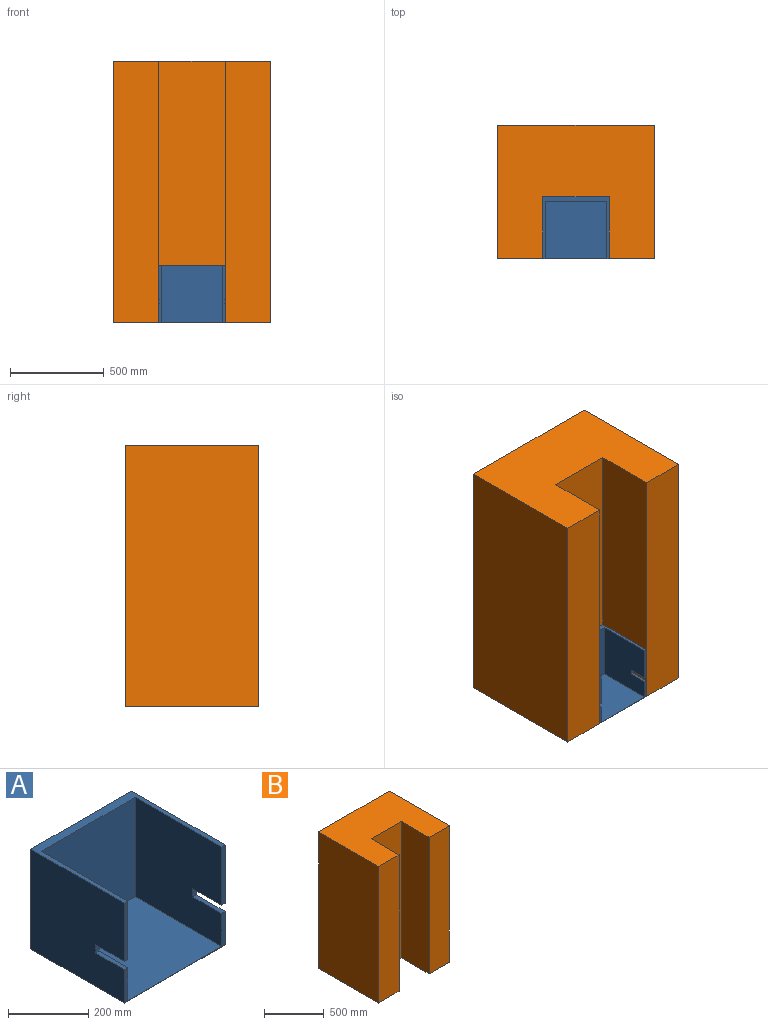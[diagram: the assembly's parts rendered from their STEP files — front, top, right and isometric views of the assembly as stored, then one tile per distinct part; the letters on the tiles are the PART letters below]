
ASSEMBLY  parts=2 mates=1
PART A: 18 faces, bbox 355.6x330.2x304.8 mm
  f0: plane 177.8x12.7mm, normal (0,-1,0), area 2258.1mm2, adj f2,f3,f11,f16
  f1: plane 177.8x12.7mm, normal (0,-1,0), area 2258.1mm2, adj f4,f5,f11,f13
  f2: plane 330.2x304.8mm, normal (1,0,0), area 98064.3mm2, adj f0,f6,f7,f9,f11,f15,f16,f17
  f3: plane 304.8x303.21mm, normal (-1,0,0), area 89838.5mm2, adj f0,f6,f8,f10,f11,f15,f16,f17
  f4: plane 304.8x303.21mm, normal (1,0,0), area 89838.5mm2, adj f1,f6,f8,f10,f11,f12,f13,f14
  f5: plane 330.2x304.8mm, normal (-1,0,0), area 98064.3mm2, adj f1,f6,f7,f9,f11,f12,f13,f14
  f6: plane 355.6x101.6mm, normal (0,-1,0), area 3104.8mm2, adj f2,f3,f4,f5,f8,f9,f14,f15
  f7: plane 355.6x304.8mm, normal (0,1,0), area 108386.9mm2, adj f2,f5,f9,f11
  f8: plane 330.2x304.8mm, normal (0,0,1), area 100645mm2, adj f3,f4,f6,f10
  f9: plane 355.6x330.2mm, normal (0,0,-1), area 117419.1mm2, adj f2,f5,f6,f7
  f10: plane 330.2x303.21mm, normal (0,-1,0), area 100120.8mm2, adj f3,f4,f8,f11
  f11: plane 355.6x330.2mm, normal (0,0,1), area 16774.2mm2, adj f0,f1,f2,f3,f4,f5,f7,f10
  f12: plane 25.4x12.7mm, normal (0,-1,0), area 322.6mm2, adj f4,f5,f13,f14
  f13: plane 101.6x12.7mm, normal (0,0,-1), area 1290.3mm2, adj f1,f4,f5,f12
  f14: plane 101.6x12.7mm, normal (0,0,1), area 1290.3mm2, adj f4,f5,f6,f12
  f15: plane 101.6x12.7mm, normal (0,0,1), area 1290.3mm2, adj f2,f3,f6,f17
  f16: plane 101.6x12.7mm, normal (0,0,-1), area 1290.3mm2, adj f0,f2,f3,f17
  f17: plane 25.4x12.7mm, normal (0,-1,0), area 322.6mm2, adj f2,f3,f15,f16
PART B: 12 faces, bbox 838.2x711.2x1397 mm
  f0: plane 1397x241.3mm, normal (0,-1,0), area 337096.1mm2, adj f1,f2,f5,f9
  f1: plane 838.2x711.2mm, normal (0,0,1), area 478708.7mm2, adj f0,f3,f4,f5,f6,f9,f10,f11
  f2: plane 838.2x711.2mm, normal (0,0,-1), area 478708.7mm2, adj f0,f3,f4,f5,f6,f9,f10,f11
  f3: plane 1397x711.2mm, normal (1,0,0), area 991519.6mm2, adj f1,f2,f4,f6,f7
  f4: plane 1397x838.2mm, normal (0,1,0), area 1170965.4mm2, adj f1,f2,f3,f5
  f5: plane 1397x711.2mm, normal (-1,0,0), area 993546.4mm2, adj f0,f1,f2,f4
  f6: plane 1397x241.3mm, normal (0,-1,0), area 337096.1mm2, adj f1,f2,f3,f10
  f7: cylinder r=25.4mm len=50.8mm, axis (1,0,0), area 4053.7mm2, adj f3,f8
  f8: plane 50.8x50.8mm, normal (1,0,0), area 2026.8mm2, adj f7
  f9: plane 1397x330.2mm, normal (1,0,0), area 461289.4mm2, adj f0,f1,f2,f11
  f10: plane 1397x330.2mm, normal (-1,0,0), area 461289.4mm2, adj f1,f2,f6,f11
  f11: plane 1397x355.6mm, normal (0,-1,0), area 496773.2mm2, adj f1,f2,f9,f10
PLACE A t=(50.31,-213.92,-460.67)mm
PLACE B t=(-466.43,-189.45,-460.67)mm
MATE planar A.f9 <-> B.f2  axis (0,0,-1) through (-91.24,80.48,-460.67)mm
